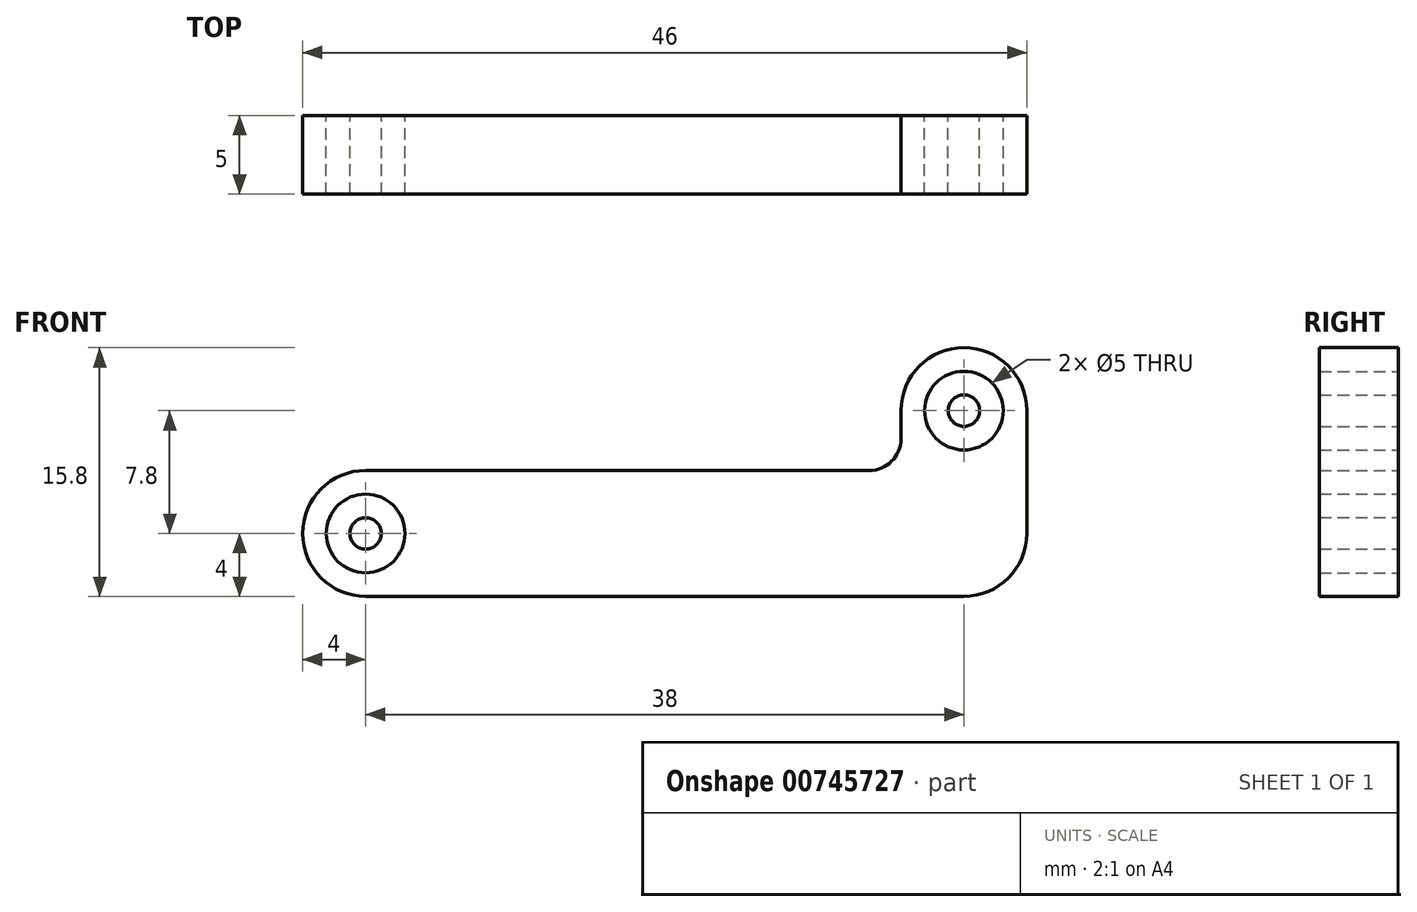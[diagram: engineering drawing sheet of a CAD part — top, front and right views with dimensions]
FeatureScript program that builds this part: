
annotation { "Feature Type Name" : "Feature", "Feature Type Description" : "" }
export const myFeature = defineFeature(function(context is Context, id is Id, definition is map)
    precondition{}
    {
        {
            var Q0;
            Q0=qCreatedBy(makeId("Front.planeOp"),FACE);
            var sketch = newSketch(context, id + "F0", { "sketchPlane" : qUnion([Q0])});
            skArc(sketch, "E0", {"start": v(42, 7.8) * mm, "mid": v(38, 11.8) * mm, "end": v(34, 7.8) * mm});
            skArc(sketch, "E1", {"start": v(0, 4) * mm, "mid": v(-4, 0) * mm, "end": v(0, -4) * mm});
            skLineSegment(sketch, "E2", {"start": v(0, 4) * mm, "end": v(32, 4) * mm});
            skLineSegment(sketch, "E3", {"start": v(34, 7.8) * mm, "end": v(34, 6) * mm});
            skLineSegment(sketch, "E4", {"start": v(42, 7.8) * mm, "end": v(42, 0) * mm});
            skLineSegment(sketch, "E5", {"start": v(0, -4) * mm, "end": v(38, -4) * mm});
            skPoint(sketch, "E6.visualSharp", {"position": v(34, 4) * mm});
            skArc(sketch, "E6.filletArc", {"start": v(32, 4) * mm, "mid": v(33.41, 4.59) * mm, "end": v(34, 6) * mm});
            skPoint(sketch, "E7.visualSharp", {"position": v(42, -4) * mm});
            skArc(sketch, "E7.filletArc", {"start": v(38, -4) * mm, "mid": v(40.83, -2.83) * mm, "end": v(42, 0) * mm});
            skCircle(sketch, "E8", {"center": v(0, 0) * mm, "radius": 2.5 * mm});
            skCircle(sketch, "E9", {"center": v(0, 0) * mm, "radius": 1 * mm});
            skCircle(sketch, "E10", {"center": v(38, 7.8) * mm, "radius": 2.5 * mm});
            skCircle(sketch, "E11", {"center": v(38, 7.8) * mm, "radius": 1 * mm});
            skSolve(sketch);
        }
        {
            var Q0;
            Q0 = qSketchRegion(id + "F0", true);
            var Q1;
            Q1=makeQuery(id+"F0.imprint","IMPRINT",FACE,{"disambiguationData":[TD([[makeQuery(id+"F0.imprint","IMPRINT",EDGE,{"derivedFrom":sQuery(id+"F0.wireOp",EDGE,"E9")}),1.0]])]});
            var Q2;
            Q2=makeQuery(id+"F0.imprint","IMPRINT",FACE,{"disambiguationData":[TD([[makeQuery(id+"F0.imprint","IMPRINT",EDGE,{"derivedFrom":sQuery(id+"F0.wireOp",EDGE,"E11")}),1.0]])]});
            extrude(context, id + "F1", {"entities" : qUnion([Q0, Q1, Q2]), "depth" : 5 * mm, "offsetDistance" : 25.4 * mm});
        }
    });
